# Revit family: FU_Table_Sandler_HDS Desk 24
name_source: partatom
category: Furniture
units: mm (PartAtom-declared; Revit-internal decimal feet)

## family parameters
Always vertical = Yes
Cut with Voids When Loaded = No
OmniClass Number = 23.40.20.00
OmniClass Title = General Furniture and Specialties
Room Calculation Point = No
Shared = No
Work Plane-Based = No

## types (1)
- HDS Desk24
    Default Elevation = 0 mm  [stored 0 ft]
    Depth = 540 mm  [stored 1.77165 ft]
    Description = HDS High Density Stacking Desk with metal frame and tops in HPL Laminate, Fenix Laminate or Natural Oak or Walnut. The desk stacks up to 30 on a trolley
    Height = 730 mm  [stored 2.39501 ft]
    Manufacturer = Sandler
    Model = HDS Desk24
    URL = https://www.sandlerseating.com
    Width = 690 mm  [stored 2.26378 ft]

note: [stored X ft] marks values corroborated as IEEE doubles in the binary element streams (Revit-internal decimal feet)

## geometry (parser evidence)
native form markers: Sweep x3
no freeform markers — native parametric forms only
